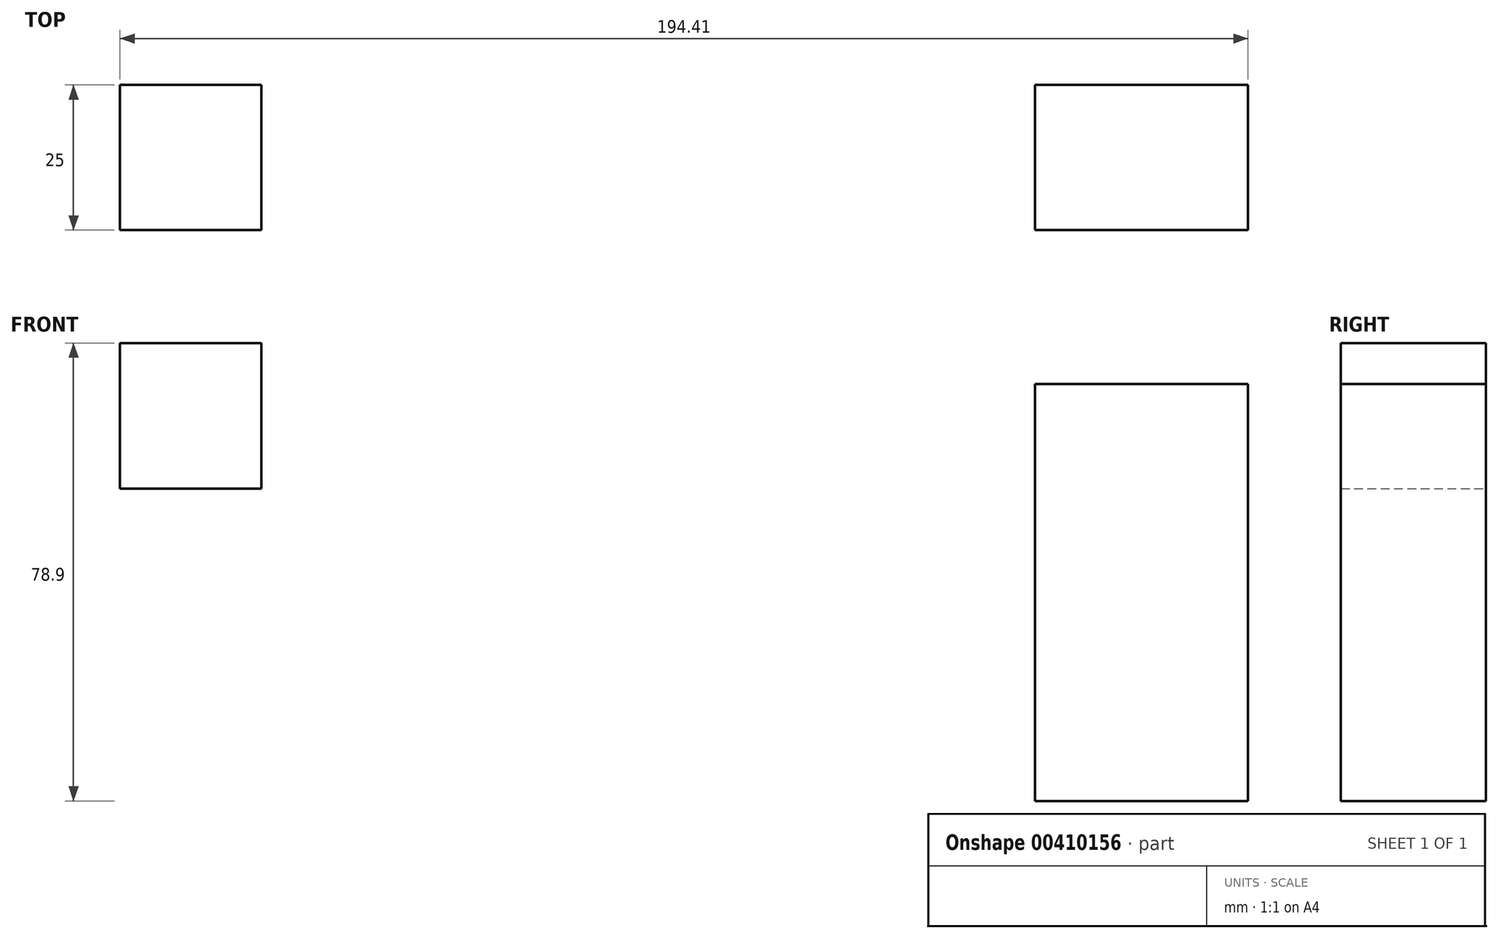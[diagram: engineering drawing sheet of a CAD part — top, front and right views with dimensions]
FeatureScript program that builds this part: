
annotation { "Feature Type Name" : "Feature", "Feature Type Description" : "" }
export const myFeature = defineFeature(function(context is Context, id is Id, definition is map)
    precondition{}
    {
        {
            var Q0;
            Q0=qCreatedBy(makeId("Front.planeOp"),FACE);
            var sketch = newSketch(context, id + "F0", { "sketchPlane" : qUnion([Q0])});
            skLineSegment(sketch, "E0.bottom", {"start": v(-94.77, 12.24) * mm, "end": v(-70.43, 12.24) * mm});
            skLineSegment(sketch, "E0.top", {"start": v(-94.77, -12.87) * mm, "end": v(-70.43, -12.87) * mm});
            skLineSegment(sketch, "E0.left", {"start": v(-94.77, 12.24) * mm, "end": v(-94.77, -12.87) * mm});
            skLineSegment(sketch, "E0.right", {"start": v(-70.43, 12.24) * mm, "end": v(-70.43, -12.87) * mm});
            skLineSegment(sketch, "E1.bottom", {"start": v(62.96, 5.2) * mm, "end": v(99.64, 5.2) * mm});
            skLineSegment(sketch, "E1.top", {"start": v(62.96, -66.66) * mm, "end": v(99.64, -66.66) * mm});
            skLineSegment(sketch, "E1.left", {"start": v(62.96, 5.2) * mm, "end": v(62.96, -66.66) * mm});
            skLineSegment(sketch, "E1.right", {"start": v(99.64, 5.2) * mm, "end": v(99.64, -66.66) * mm});
            skSolve(sketch);
        }
        {
            var Q0;
            Q0 = qSketchRegion(id + "F0", true);
            extrude(context, id + "F1", {"entities" : qUnion([Q0]), "depth" : 25 * mm});
        }
    });
